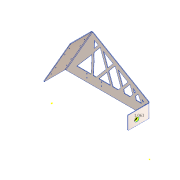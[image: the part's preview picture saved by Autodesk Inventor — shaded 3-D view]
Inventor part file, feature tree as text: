
AUTODESK INVENTOR PART (.ipt)
format: ipt  version: 2016 (Build 200138000, 138)  size: 391,168 bytes
history: native  units: in
note: dims shown in document units (in); Inventor stores cm internally (conversion verified against a paired STEP export)
features: sheet_metal_op x11, sketch x11, reference x11, other x9, hole x2, fillet x1, projected_geometry x1
ambient origin geometry x8: Origin, YZ Plane, XZ Plane, XY Plane, X Axis, Y Axis, Z Axis, Center Point
bodies: Solid1 (feature_tree)
feature tree (46):
  sheet_metal_op  "Face1"
  sheet_metal_op  "Flange1"
  sketch  "Sketch5"  dims[d10=90.0deg]
  sheet_metal_op  "Flange2"
  fillet  "Fillet1"  Radius=30.0in
  sketch  "Sketch7"  dims[d12=0.125in]
  hole  "Hole1"  [1 undecoded]
  sketch  "Sketch9"  dims[d14=0.125in]
  hole  "Hole2"  [1 undecoded]
  sketch  "Sketch13"  dims[d17=0.125in d18=5.0in d19=-0.6184in d20=0.125in d21=0.5in d22=0.125in d23=0.125in d24=0.125in d25=0.0625in d26=0.25in d27=0.125in d28=5.0in d29=-0.6184in d30=0.125in d31=0.5in d32=0.125in d33=0.125in d36=1.063in d37=0.125in d38=0.0in d39=0.125in d40=0.19in d41=0.75in d42=0.375in d43=0.25in d44=0.5635in d45=0.125in d46=0.8108in d52=0.125in d53=0.0in d54=2.0in d56=2.0in d57=2.0in d58=2.0in d59=0.19in d60=0.75in d61=0.375in d62=0.25in d63=0.5635in d64=0.125in d65=0.8108in d66=0.125in d67=0.125in d68=0.0625in d69=0.25in d70=0.125in d71=0.125in d72=0.125in d73=0.0625in d74=0.25in d75=0.125in]
  sheet_metal_op  "Face2"
  sheet_metal_op  "Face3"
  sketch  "Sketch1"  dims[d1=30.0in d2=0.125in]
  other  "Plate1"
  sketch  "Sketch3"  dims[d7=60.0deg d8=3.0in]
  reference  "Reference12"
  reference  "Reference13"
  reference  "Reference14"
  sketch  "Sketch4"  dims[d9=180.0deg]
  other  "Plate2"
  sheet_metal_op  "Bend1"
  sheet_metal_op  "Corner1"
  reference  "Reference15"
  reference  "Reference16"
  reference  "Reference17"
  sketch  "Sketch6"  dims[d11=13.0167in]
  other  "Plate3"
  sheet_metal_op  "Bend2"
  sheet_metal_op  "Corner2"
  reference  "Reference18"
  reference  "Reference19"
  reference  "Reference20"
  reference  "Reference21"
  reference  "Reference22"
  sketch  "Sketch8"  dims[d13=0.0in]
  sketch  "Sketch10"  dims[d15=0.0625in]
  sketch  "Sketch11"  dims[d16=0.25in]
  projected_geometry  "Projected Loop1"
  other  "Plate4"
  sheet_metal_op  "Bend3"
  other  "Plate5"
  sheet_metal_op  "Bend4"
  other  "Cut1"
  other  "Cut2"
  other  "Cut3"
  other  "Definition1"
note: 2 required parameter values undecoded (feature->parameter linkage not recoverable at this tier; creation-order binding heuristic only, values carry confidence <= 0.55)
